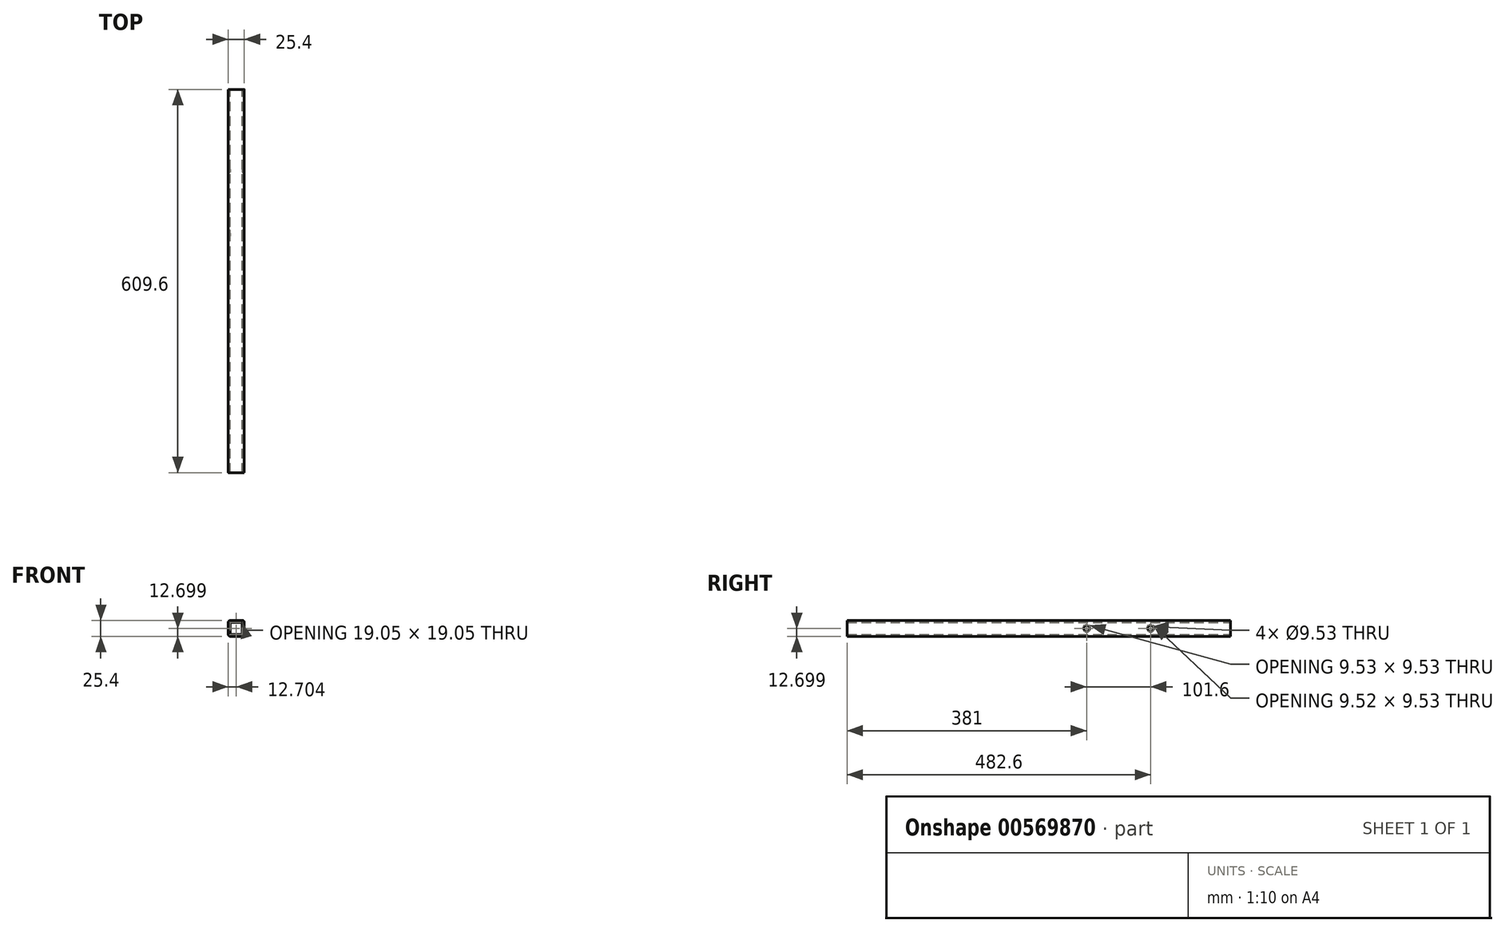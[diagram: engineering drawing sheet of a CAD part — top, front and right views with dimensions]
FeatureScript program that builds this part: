
annotation { "Feature Type Name" : "Feature", "Feature Type Description" : "" }
export const myFeature = defineFeature(function(context is Context, id is Id, definition is map)
    precondition{}
    {
        {
            var Q0;
            Q0=qCreatedBy(makeId("Front.planeOp"),FACE);
            var sketch = newSketch(context, id + "F0", { "sketchPlane" : qUnion([Q0])});
            skLineSegment(sketch, "E0.bottom", {"start": v(9.13, -11.87) * mm, "end": v(-9.92, -11.87) * mm});
            skLineSegment(sketch, "E0.top", {"start": v(9.13, 13.53) * mm, "end": v(-9.92, 13.53) * mm});
            skLineSegment(sketch, "E0.left", {"start": v(12.3, -8.7) * mm, "end": v(12.3, 10.35) * mm});
            skLineSegment(sketch, "E0.right", {"start": v(-13.1, -8.7) * mm, "end": v(-13.1, 10.35) * mm});
            skLineSegment(sketch, "E1.bottom", {"start": v(5.95, -8.7) * mm, "end": v(-6.75, -8.7) * mm});
            skLineSegment(sketch, "E1.top", {"start": v(5.95, 10.35) * mm, "end": v(-6.75, 10.35) * mm});
            skLineSegment(sketch, "E1.left", {"start": v(9.13, -5.52) * mm, "end": v(9.13, 7.18) * mm});
            skLineSegment(sketch, "E1.right", {"start": v(-9.92, -5.52) * mm, "end": v(-9.92, 7.18) * mm});
            skPoint(sketch, "E2.visualSharp", {"position": v(9.13, 10.35) * mm});
            skArc(sketch, "E2.filletArc", {"start": v(9.13, 7.18) * mm, "mid": v(8.2, 9.42) * mm, "end": v(5.95, 10.35) * mm});
            skPoint(sketch, "E3.visualSharp", {"position": v(-9.92, 10.35) * mm});
            skArc(sketch, "E3.filletArc", {"start": v(-6.75, 10.35) * mm, "mid": v(-9, 9.42) * mm, "end": v(-9.92, 7.18) * mm});
            skPoint(sketch, "E4.visualSharp", {"position": v(-9.92, -8.7) * mm});
            skArc(sketch, "E4.filletArc", {"start": v(-9.92, -5.52) * mm, "mid": v(-9, -7.77) * mm, "end": v(-6.75, -8.7) * mm});
            skPoint(sketch, "E5.visualSharp", {"position": v(9.13, -8.7) * mm});
            skArc(sketch, "E5.filletArc", {"start": v(5.95, -8.7) * mm, "mid": v(8.2, -7.77) * mm, "end": v(9.13, -5.52) * mm});
            skPoint(sketch, "E6.visualSharp", {"position": v(12.3, 13.53) * mm});
            skArc(sketch, "E6.filletArc", {"start": v(12.3, 10.35) * mm, "mid": v(11.37, 12.6) * mm, "end": v(9.13, 13.53) * mm});
            skPoint(sketch, "E7.visualSharp", {"position": v(-13.1, 13.53) * mm});
            skArc(sketch, "E7.filletArc", {"start": v(-9.92, 13.53) * mm, "mid": v(-12.17, 12.6) * mm, "end": v(-13.1, 10.35) * mm});
            skPoint(sketch, "E8.visualSharp", {"position": v(-13.1, -11.87) * mm});
            skArc(sketch, "E8.filletArc", {"start": v(-13.1, -8.7) * mm, "mid": v(-12.17, -10.94) * mm, "end": v(-9.92, -11.87) * mm});
            skPoint(sketch, "E9.visualSharp", {"position": v(12.3, -11.87) * mm});
            skArc(sketch, "E9.filletArc", {"start": v(9.13, -11.87) * mm, "mid": v(11.37, -10.94) * mm, "end": v(12.3, -8.7) * mm});
            skSolve(sketch);
        }
        {
            var Q0;
            Q0 = qSketchRegion(id + "F0", true);
            extrude(context, id + "F1", {"entities" : qUnion([Q0]), "depth" : 609.6 * mm, "offsetDistance" : 25.4 * mm});
        }
        {
            var Q0;
            Q0=makeQuery(id+"F1.opExtrude","SWEPT_FACE",FACE,{"disambiguationData":[OSD([sQuery(id+"F0.wireOp",EDGE,"E0.left")])]});
            var sketch = newSketch(context, id + "F2", { "sketchPlane" : qUnion([Q0])});
            skCircle(sketch, "E10", {"center": v(-228.6, 0.83) * mm, "radius": 4.76 * mm});
            skCircle(sketch, "E11", {"center": v(-127, 0.83) * mm, "radius": 4.76 * mm});
            skSolve(sketch);
        }
        {
            var Q0;
            Q0 = qSketchRegion(id + "F2", true);
            extrude(context, id + "F3", {"entities" : qUnion([Q0]), "operationType" : NewBodyOperationType.REMOVE, "oppositeDirection" : true, "depth" : 25.4 * mm, "offsetDistance" : 25.4 * mm});
        }
    });
